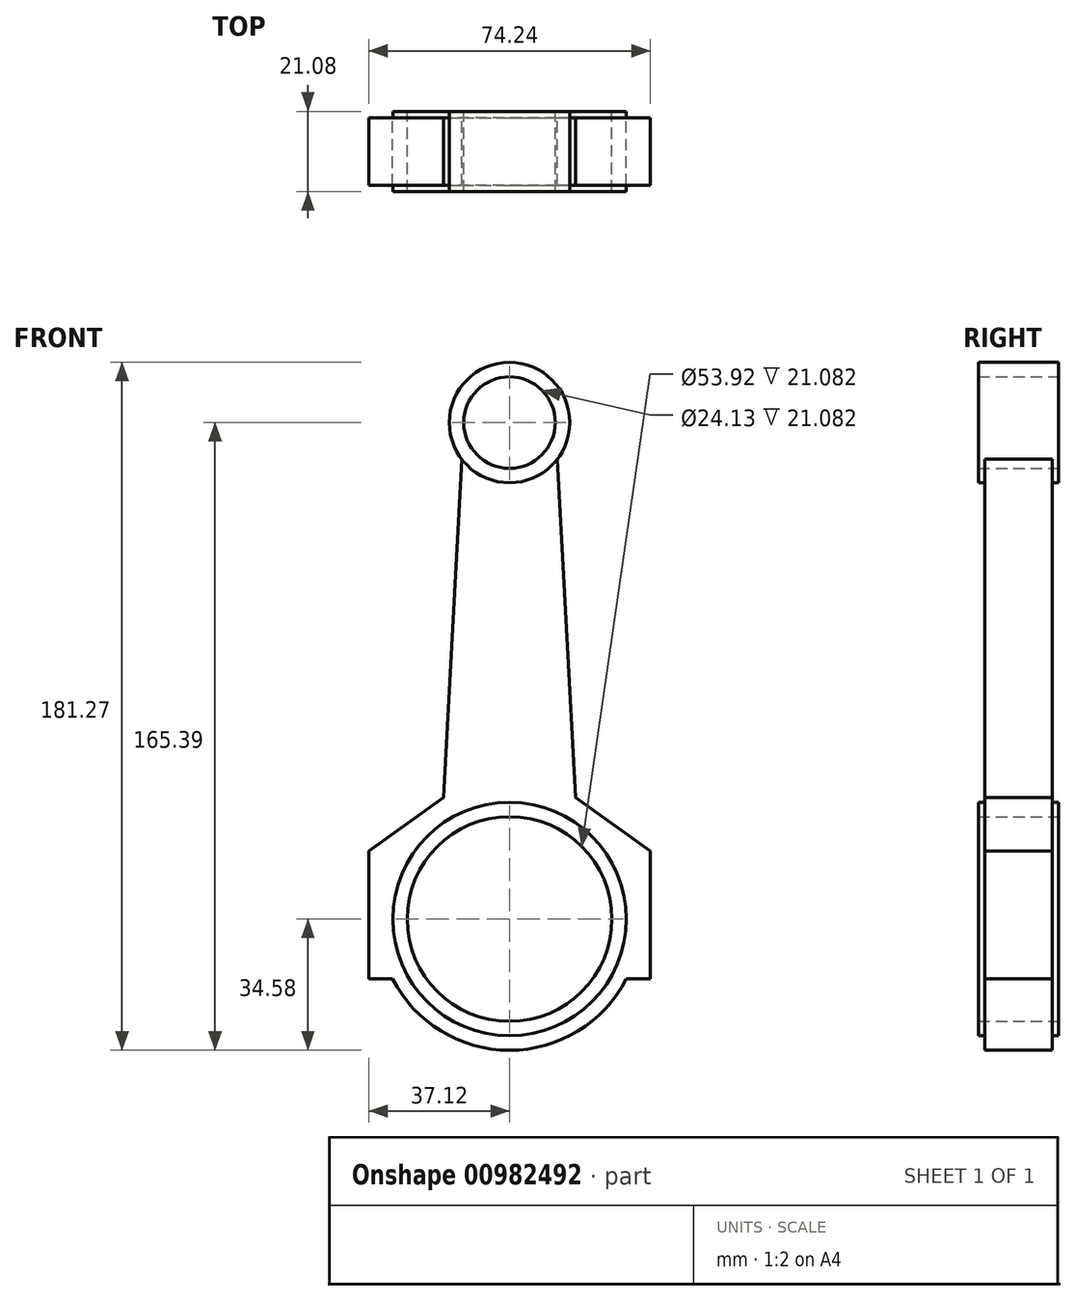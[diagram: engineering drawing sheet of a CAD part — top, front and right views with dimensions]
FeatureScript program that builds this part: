
annotation { "Feature Type Name" : "Feature", "Feature Type Description" : "" }
export const myFeature = defineFeature(function(context is Context, id is Id, definition is map)
    precondition{}
    {
        {
            var Q0;
            Q0=qCreatedBy(makeId("Front.planeOp"),FACE);
            var sketch = newSketch(context, id + "F0", { "sketchPlane" : qUnion([Q0])});
            skCircle(sketch, "E0", {"center": v(0, -63.2) * mm, "radius": 26.96 * mm});
            skLineSegment(sketch, "E1", {"start": v(0, -63.2) * mm, "end": v(0, 67.61) * mm, "construction": true});
            skCircle(sketch, "E2", {"center": v(0, 67.61) * mm, "radius": 12.06 * mm});
            skCircle(sketch, "E3.0", {"center": v(0, 67.61) * mm, "radius": 15.88 * mm});
            skCircle(sketch, "E4.0", {"center": v(0, -63.2) * mm, "radius": 30.77 * mm});
            skArc(sketch, "E5.0", {"start": v(-30.8, -78.92) * mm, "mid": v(0, -97.78) * mm, "end": v(30.8, -78.92) * mm});
            skLineSegment(sketch, "E6", {"start": v(0, -63.2) * mm, "end": v(-37.12, -63.2) * mm});
            skLineSegment(sketch, "E7", {"start": v(-37.12, -63.2) * mm, "end": v(-37.12, -45.29) * mm});
            skLineSegment(sketch, "E8", {"start": v(-37.12, -45.29) * mm, "end": v(-17.35, -31.2) * mm});
            skLineSegment(sketch, "E9", {"start": v(-17.35, -31.2) * mm, "end": v(-12.6, 57.95) * mm});
            skLineSegment(sketch, "E10", {"start": v(-37.12, -63.2) * mm, "end": v(-37.12, -78.92) * mm});
            skLineSegment(sketch, "E11", {"start": v(-37.12, -78.92) * mm, "end": v(-30.8, -78.92) * mm});
            skLineSegment(sketch, "E12.MirrorCS", {"start": v(17.35, -31.2) * mm, "end": v(12.6, 57.95) * mm});
            skLineSegment(sketch, "E13.MirrorCS", {"start": v(37.12, -45.29) * mm, "end": v(17.35, -31.2) * mm});
            skLineSegment(sketch, "E14.MirrorCS", {"start": v(37.12, -63.2) * mm, "end": v(37.12, -45.29) * mm});
            skLineSegment(sketch, "E15.MirrorCS", {"start": v(37.12, -78.92) * mm, "end": v(30.8, -78.92) * mm});
            skLineSegment(sketch, "E16.MirrorCS", {"start": v(37.12, -63.2) * mm, "end": v(37.12, -78.92) * mm});
            skLineSegment(sketch, "E17.MirrorCS", {"start": v(0, -63.2) * mm, "end": v(37.12, -63.2) * mm});
            skPoint(sketch, "E18.orphan", {"position": v(-12.05, 68.25) * mm});
            skPoint(sketch, "E19.orphan", {"position": v(12.05, 68.25) * mm});
            skSolve(sketch);
        }
        {
            var Q0;
            {var subQ0=sQuery(id+"F0.wireOp",EDGE,"E6");var subQ1=sQuery(id+"F0.wireOp",EDGE,"E0");var subQ2=makeQuery(id+"F0.imprint","INTERSECT",VERTEX,{"derivedFrom":[subQ1,subQ0]});Q0=makeQuery(id+"F0.imprint","IMPRINT",FACE,{"disambiguationData":[TD([[makeQuery(id+"F0.imprint","IMPRINT",EDGE,{"disambiguationData":[TD([[subQ2,1.0]])],"derivedFrom":subQ1}),-1.0]])]});}
            extrude(context, id + "F1", {"entities" : qUnion([Q0]), "endBound" : BoundingType.SYMMETRIC, "depth" : 21.08 * mm, "offsetDistance" : 25.4 * mm});
        }
        {
            var Q0;
            {var subQ0=sQuery(id+"F0.wireOp",EDGE,"E7");Q0=makeQuery(id+"F0.imprint","IMPRINT",FACE,{"disambiguationData":[TD([[makeQuery(id+"F0.imprint","IMPRINT",EDGE,{"derivedFrom":subQ0}),-1.0]])]});}
            extrude(context, id + "F2", {"entities" : qUnion([Q0]), "operationType" : NewBodyOperationType.ADD, "endBound" : BoundingType.SYMMETRIC, "depth" : 17.78 * mm, "offsetDistance" : 25.4 * mm});
        }
        {
            var Q0;
            {var subQ0=sQuery(id+"F0.wireOp",EDGE,"E6");var subQ1=sQuery(id+"F0.wireOp",EDGE,"E0");var subQ2=makeQuery(id+"F0.imprint","INTERSECT",VERTEX,{"derivedFrom":[subQ1,subQ0]});Q0=makeQuery(id+"F0.imprint","IMPRINT",FACE,{"disambiguationData":[TD([[makeQuery(id+"F0.imprint","IMPRINT",EDGE,{"disambiguationData":[TD([[subQ2,-1.0]])],"derivedFrom":subQ1}),-1.0]])]});}
            extrude(context, id + "F3", {"entities" : qUnion([Q0]), "endBound" : BoundingType.SYMMETRIC, "depth" : 21.08 * mm, "offsetDistance" : 25.4 * mm});
        }
        {
            var Q0;
            Q0=makeQuery(id+"F0.imprint","IMPRINT",FACE,{"disambiguationData":[TD([[makeQuery(id+"F0.imprint","IMPRINT",EDGE,{"derivedFrom":sQuery(id+"F0.wireOp",EDGE,"E5.0")}),1.0]])]});
            extrude(context, id + "F4", {"entities" : qUnion([Q0]), "operationType" : NewBodyOperationType.ADD, "endBound" : BoundingType.SYMMETRIC, "depth" : 17.78 * mm, "offsetDistance" : 25.4 * mm});
        }
        {
            var Q0;
            Q0=makeQuery(id+"F0.imprint","IMPRINT",FACE,{"disambiguationData":[TD([[makeQuery(id+"F0.imprint","IMPRINT",EDGE,{"derivedFrom":sQuery(id+"F0.wireOp",EDGE,"E2")}),-1.0]])]});
            extrude(context, id + "F5", {"entities" : qUnion([Q0]), "operationType" : NewBodyOperationType.ADD, "endBound" : BoundingType.SYMMETRIC, "depth" : 21.08 * mm, "offsetDistance" : 25.4 * mm});
        }
    });
